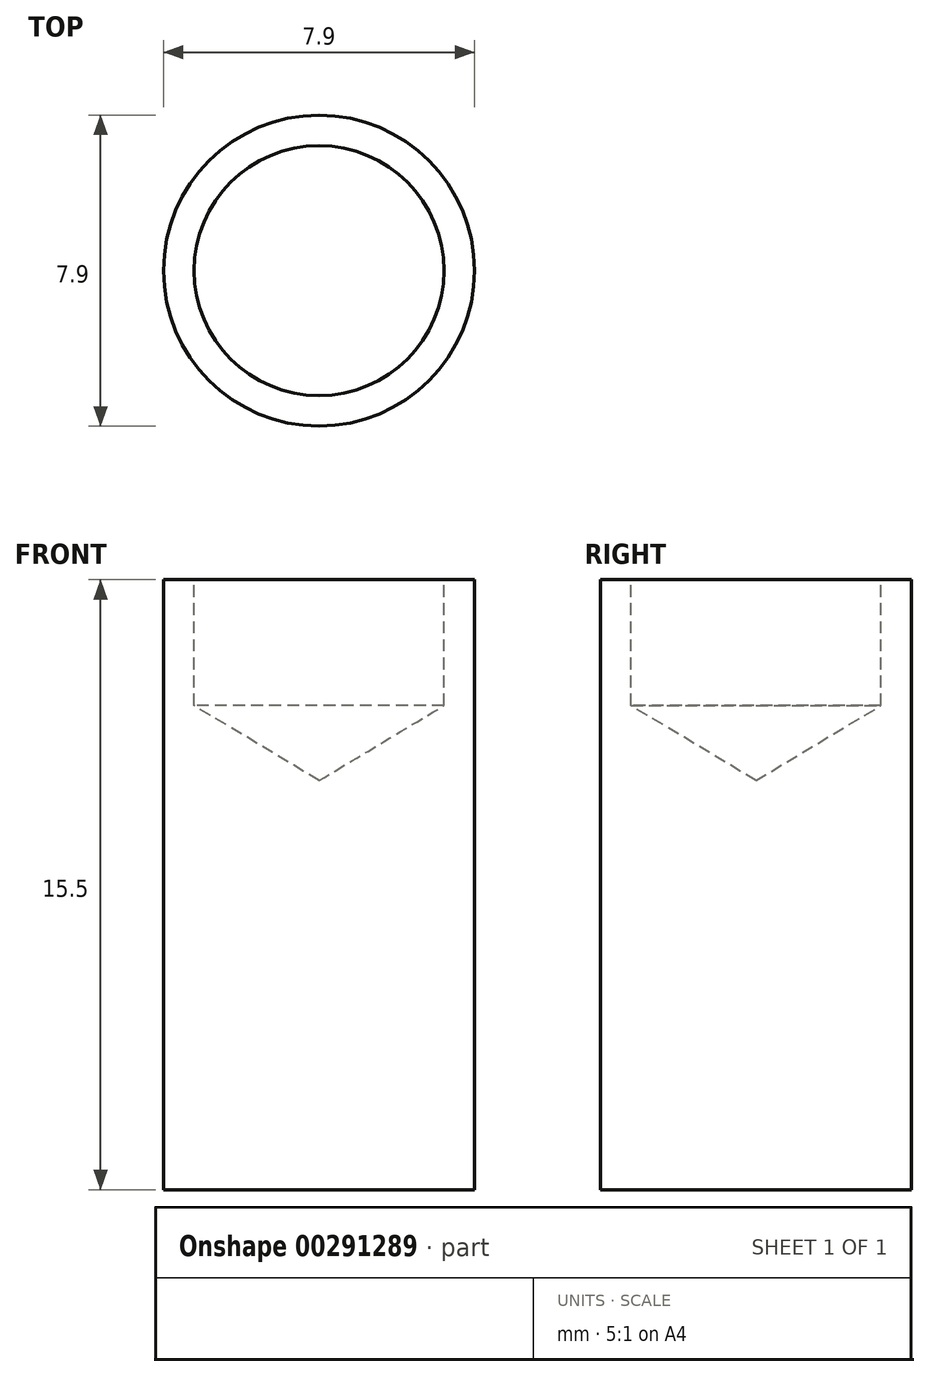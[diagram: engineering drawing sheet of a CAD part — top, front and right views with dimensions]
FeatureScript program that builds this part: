
annotation { "Feature Type Name" : "Feature", "Feature Type Description" : "" }
export const myFeature = defineFeature(function(context is Context, id is Id, definition is map)
    precondition{}
    {
        {
            var Q0;
            Q0=qCreatedBy(makeId("Top.planeOp"),FACE);
            var sketch = newSketch(context, id + "F0", { "sketchPlane" : qUnion([Q0])});
            skCircle(sketch, "E0", {"center": v(0, 0) * mm, "radius": 3.95 * mm});
            skSolve(sketch);
        }
        {
            var Q0;
            Q0=makeQuery(id+"F0.imprint","IMPRINT",FACE,{"disambiguationData":[TD([[makeQuery(id+"F0.imprint","IMPRINT",EDGE,{"derivedFrom":sQuery(id+"F0.wireOp",EDGE,"E0")}),1.0]])]});
            var Q1;
            Q1=sQuery(id+"F0.wireOp",EDGE,"E0");
            extrude(context, id + "F1", {"entities" : qUnion([Q0]), "surfaceEntities" : qUnion([Q1]), "depth" : 15.5 * mm});
        }
        {
            var Q0;
            Q0=makeQuery(id+"F1.opExtrude","CAP_FACE",FACE,{"disambiguationData":[OSD([sQuery(id+"F0.wireOp",EDGE,"E0")])],"isStart":false});
            var sketch = newSketch(context, id + "F2", { "sketchPlane" : qUnion([Q0])});
            skCircle(sketch, "E1", {"center": v(0, 0) * mm, "radius": 3.17 * mm});
            skSolve(sketch);
        }
        {
            var Q0;
            Q0=sQuery(id+"F2.wireOp",VERTEX,"E1.center");
            var Q1;
            Q1=makeQuery(id+"F1.opExtrude","SWEPT_BODY",BODY,{"disambiguationData":[OSD([sQuery(id+"F0.wireOp",EDGE,"E0")])]});
            hole(context, id + "F3", {"style" : HoleStyle.SIMPLE, "endStyle" : HoleEndStyle.BLIND, "holeDiameter" : 6.35 * mm, "holeDepth" : 3.2 * mm, "tappedDepth" : 12 * mm, "tapClearance" : 3, "locations" : qUnion([Q0]), "scope" : qUnion([Q1])});
        }
    });
